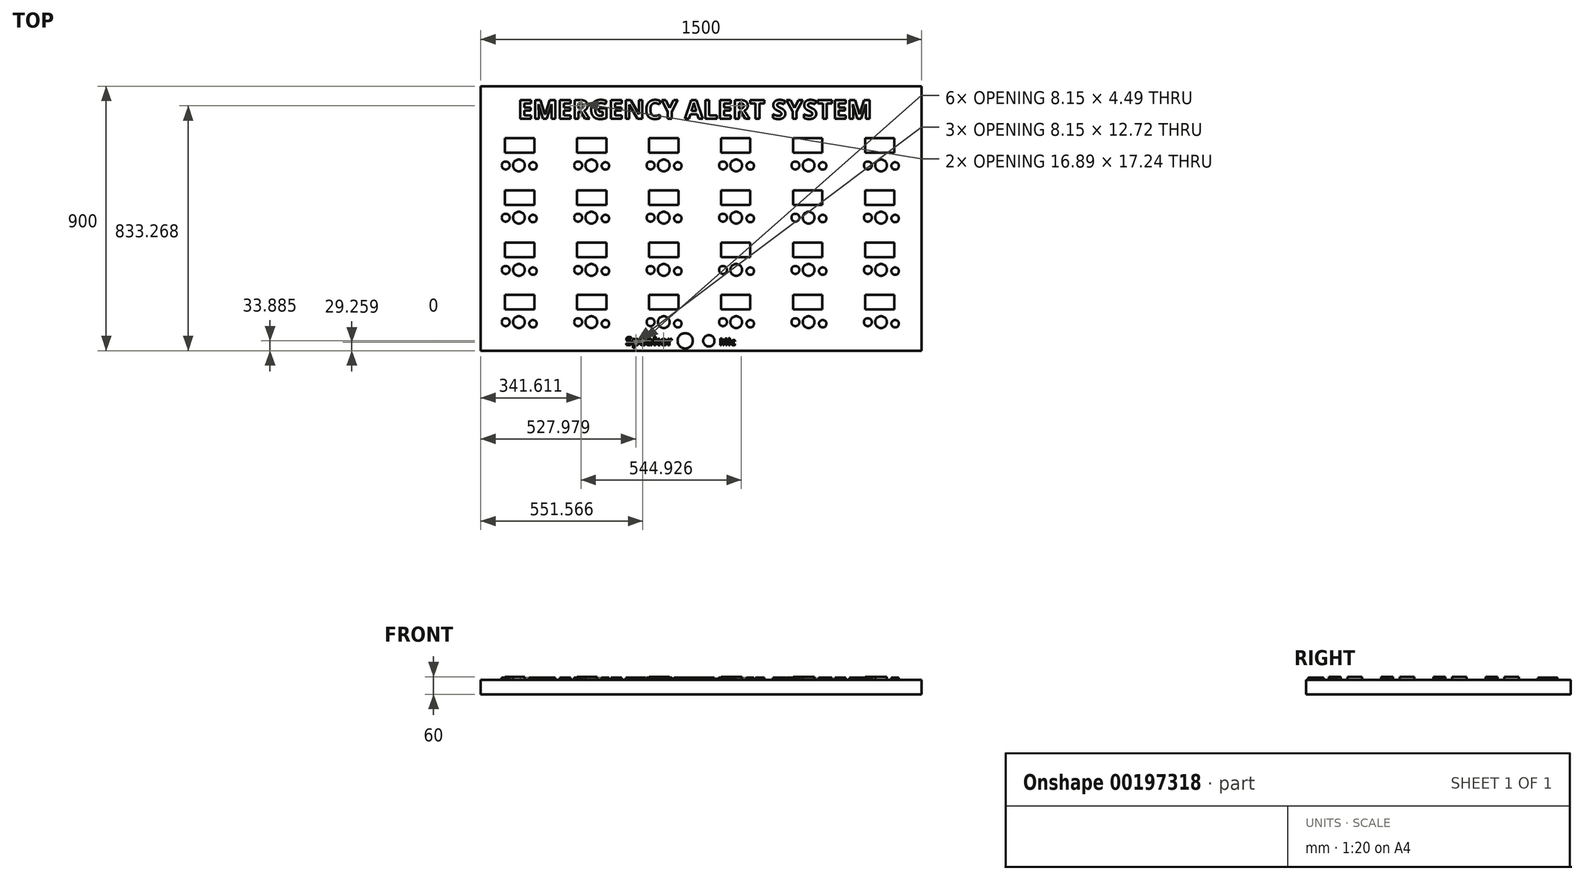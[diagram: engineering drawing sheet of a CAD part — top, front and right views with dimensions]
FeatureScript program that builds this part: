
annotation { "Feature Type Name" : "Feature", "Feature Type Description" : "" }
export const myFeature = defineFeature(function(context is Context, id is Id, definition is map)
    precondition{}
    {
        {
            var Q0;
            Q0=qCreatedBy(makeId("Top.planeOp"),FACE);
            var sketch = newSketch(context, id + "F0", { "sketchPlane" : qUnion([Q0])});
            skLineSegment(sketch, "E0.bottom", {"start": v(-750, 450) * mm, "end": v(750, 450) * mm});
            skLineSegment(sketch, "E0.top", {"start": v(-750, -450) * mm, "end": v(750, -450) * mm});
            skLineSegment(sketch, "E0.left", {"start": v(-750, 450) * mm, "end": v(-750, -450) * mm});
            skLineSegment(sketch, "E0.right", {"start": v(750, 450) * mm, "end": v(750, -450) * mm});
            skPoint(sketch, "E0.middle", {"position": v(0, 0) * mm});
            skSolve(sketch);
        }
        {
            var Q0;
            Q0=makeQuery(id+"F0.imprint","IMPRINT",FACE,{"disambiguationData":[TD([[makeQuery(id+"F0.imprint","IMPRINT",EDGE,{"derivedFrom":sQuery(id+"F0.wireOp",EDGE,"E0.bottom")}),-1.0]])]});
            extrude(context, id + "F1", {"entities" : qUnion([Q0]), "depth" : 50 * mm});
        }
        {
            var Q0;
            Q0=makeQuery(id+"F1.opExtrude","CAP_FACE",FACE,{"disambiguationData":[OSD([sQuery(id+"F0.wireOp",EDGE,"E0.bottom"),sQuery(id+"F0.wireOp",EDGE,"E0.top"),sQuery(id+"F0.wireOp",EDGE,"E0.left"),sQuery(id+"F0.wireOp",EDGE,"E0.right")])],"isStart":false});
            var sketch = newSketch(context, id + "F2", { "sketchPlane" : qUnion([Q0])});
            skLineSegment(sketch, "E1.bottom", {"start": v(-667.65, 273.63) * mm, "end": v(-567.65, 273.63) * mm});
            skLineSegment(sketch, "E1.top", {"start": v(-667.65, 223.63) * mm, "end": v(-567.65, 223.63) * mm});
            skLineSegment(sketch, "E1.left", {"start": v(-667.65, 273.63) * mm, "end": v(-667.65, 223.63) * mm});
            skLineSegment(sketch, "E1.right", {"start": v(-567.65, 273.63) * mm, "end": v(-567.65, 223.63) * mm});
            skLineSegment(sketch, "E2.0.1.0", {"start": v(-667.65, 95.83) * mm, "end": v(-567.65, 95.83) * mm});
            skLineSegment(sketch, "E2.0.1.1", {"start": v(-567.65, 95.83) * mm, "end": v(-567.65, 45.83) * mm});
            skLineSegment(sketch, "E2.0.1.2", {"start": v(-667.65, 45.83) * mm, "end": v(-567.65, 45.83) * mm});
            skLineSegment(sketch, "E2.0.1.3", {"start": v(-667.65, 95.83) * mm, "end": v(-667.65, 45.83) * mm});
            skLineSegment(sketch, "E2.0.2.0", {"start": v(-667.65, -81.97) * mm, "end": v(-567.65, -81.97) * mm});
            skLineSegment(sketch, "E2.0.2.1", {"start": v(-567.65, -81.97) * mm, "end": v(-567.65, -131.97) * mm});
            skLineSegment(sketch, "E2.0.2.2", {"start": v(-667.65, -131.97) * mm, "end": v(-567.65, -131.97) * mm});
            skLineSegment(sketch, "E2.0.2.3", {"start": v(-667.65, -81.97) * mm, "end": v(-667.65, -131.97) * mm});
            skLineSegment(sketch, "E2.0.3.0", {"start": v(-667.65, -259.77) * mm, "end": v(-567.65, -259.77) * mm});
            skLineSegment(sketch, "E2.0.3.1", {"start": v(-567.65, -259.77) * mm, "end": v(-567.65, -309.77) * mm});
            skLineSegment(sketch, "E2.0.3.2", {"start": v(-667.65, -309.77) * mm, "end": v(-567.65, -309.77) * mm});
            skLineSegment(sketch, "E2.0.3.3", {"start": v(-667.65, -259.77) * mm, "end": v(-667.65, -309.77) * mm});
            skLineSegment(sketch, "E2.1.0.0", {"start": v(-422.65, 273.63) * mm, "end": v(-322.65, 273.63) * mm});
            skLineSegment(sketch, "E2.1.0.1", {"start": v(-322.65, 273.63) * mm, "end": v(-322.65, 223.63) * mm});
            skLineSegment(sketch, "E2.1.0.2", {"start": v(-422.65, 223.63) * mm, "end": v(-322.65, 223.63) * mm});
            skLineSegment(sketch, "E2.1.0.3", {"start": v(-422.65, 273.63) * mm, "end": v(-422.65, 223.63) * mm});
            skLineSegment(sketch, "E2.1.1.0", {"start": v(-422.65, 95.83) * mm, "end": v(-322.65, 95.83) * mm});
            skLineSegment(sketch, "E2.1.1.1", {"start": v(-322.65, 95.83) * mm, "end": v(-322.65, 45.83) * mm});
            skLineSegment(sketch, "E2.1.1.2", {"start": v(-422.65, 45.83) * mm, "end": v(-322.65, 45.83) * mm});
            skLineSegment(sketch, "E2.1.1.3", {"start": v(-422.65, 95.83) * mm, "end": v(-422.65, 45.83) * mm});
            skLineSegment(sketch, "E2.1.2.0", {"start": v(-422.65, -81.97) * mm, "end": v(-322.65, -81.97) * mm});
            skLineSegment(sketch, "E2.1.2.1", {"start": v(-322.65, -81.97) * mm, "end": v(-322.65, -131.97) * mm});
            skLineSegment(sketch, "E2.1.2.2", {"start": v(-422.65, -131.97) * mm, "end": v(-322.65, -131.97) * mm});
            skLineSegment(sketch, "E2.1.2.3", {"start": v(-422.65, -81.97) * mm, "end": v(-422.65, -131.97) * mm});
            skLineSegment(sketch, "E2.1.3.0", {"start": v(-422.65, -259.77) * mm, "end": v(-322.65, -259.77) * mm});
            skLineSegment(sketch, "E2.1.3.1", {"start": v(-322.65, -259.77) * mm, "end": v(-322.65, -309.77) * mm});
            skLineSegment(sketch, "E2.1.3.2", {"start": v(-422.65, -309.77) * mm, "end": v(-322.65, -309.77) * mm});
            skLineSegment(sketch, "E2.1.3.3", {"start": v(-422.65, -259.77) * mm, "end": v(-422.65, -309.77) * mm});
            skLineSegment(sketch, "E2.2.0.0", {"start": v(-177.65, 273.63) * mm, "end": v(-77.65, 273.63) * mm});
            skLineSegment(sketch, "E2.2.0.1", {"start": v(-77.65, 273.63) * mm, "end": v(-77.65, 223.63) * mm});
            skLineSegment(sketch, "E2.2.0.2", {"start": v(-177.65, 223.63) * mm, "end": v(-77.65, 223.63) * mm});
            skLineSegment(sketch, "E2.2.0.3", {"start": v(-177.65, 273.63) * mm, "end": v(-177.65, 223.63) * mm});
            skLineSegment(sketch, "E2.2.1.0", {"start": v(-177.65, 95.83) * mm, "end": v(-77.65, 95.83) * mm});
            skLineSegment(sketch, "E2.2.1.1", {"start": v(-77.65, 95.83) * mm, "end": v(-77.65, 45.83) * mm});
            skLineSegment(sketch, "E2.2.1.2", {"start": v(-177.65, 45.83) * mm, "end": v(-77.65, 45.83) * mm});
            skLineSegment(sketch, "E2.2.1.3", {"start": v(-177.65, 95.83) * mm, "end": v(-177.65, 45.83) * mm});
            skLineSegment(sketch, "E2.2.2.0", {"start": v(-177.65, -81.97) * mm, "end": v(-77.65, -81.97) * mm});
            skLineSegment(sketch, "E2.2.2.1", {"start": v(-77.65, -81.97) * mm, "end": v(-77.65, -131.97) * mm});
            skLineSegment(sketch, "E2.2.2.2", {"start": v(-177.65, -131.97) * mm, "end": v(-77.65, -131.97) * mm});
            skLineSegment(sketch, "E2.2.2.3", {"start": v(-177.65, -81.97) * mm, "end": v(-177.65, -131.97) * mm});
            skLineSegment(sketch, "E2.2.3.0", {"start": v(-177.65, -259.77) * mm, "end": v(-77.65, -259.77) * mm});
            skLineSegment(sketch, "E2.2.3.1", {"start": v(-77.65, -259.77) * mm, "end": v(-77.65, -309.77) * mm});
            skLineSegment(sketch, "E2.2.3.2", {"start": v(-177.65, -309.77) * mm, "end": v(-77.65, -309.77) * mm});
            skLineSegment(sketch, "E2.2.3.3", {"start": v(-177.65, -259.77) * mm, "end": v(-177.65, -309.77) * mm});
            skLineSegment(sketch, "E2.3.0.0", {"start": v(67.35, 273.63) * mm, "end": v(167.35, 273.63) * mm});
            skLineSegment(sketch, "E2.3.0.1", {"start": v(167.35, 273.63) * mm, "end": v(167.35, 223.63) * mm});
            skLineSegment(sketch, "E2.3.0.2", {"start": v(67.35, 223.63) * mm, "end": v(167.35, 223.63) * mm});
            skLineSegment(sketch, "E2.3.0.3", {"start": v(67.35, 273.63) * mm, "end": v(67.35, 223.63) * mm});
            skLineSegment(sketch, "E2.3.1.0", {"start": v(67.35, 95.83) * mm, "end": v(167.35, 95.83) * mm});
            skLineSegment(sketch, "E2.3.1.1", {"start": v(167.35, 95.83) * mm, "end": v(167.35, 45.83) * mm});
            skLineSegment(sketch, "E2.3.1.2", {"start": v(67.35, 45.83) * mm, "end": v(167.35, 45.83) * mm});
            skLineSegment(sketch, "E2.3.1.3", {"start": v(67.35, 95.83) * mm, "end": v(67.35, 45.83) * mm});
            skLineSegment(sketch, "E2.3.2.0", {"start": v(67.35, -81.97) * mm, "end": v(167.35, -81.97) * mm});
            skLineSegment(sketch, "E2.3.2.1", {"start": v(167.35, -81.97) * mm, "end": v(167.35, -131.97) * mm});
            skLineSegment(sketch, "E2.3.2.2", {"start": v(67.35, -131.97) * mm, "end": v(167.35, -131.97) * mm});
            skLineSegment(sketch, "E2.3.2.3", {"start": v(67.35, -81.97) * mm, "end": v(67.35, -131.97) * mm});
            skLineSegment(sketch, "E2.3.3.0", {"start": v(67.35, -259.77) * mm, "end": v(167.35, -259.77) * mm});
            skLineSegment(sketch, "E2.3.3.1", {"start": v(167.35, -259.77) * mm, "end": v(167.35, -309.77) * mm});
            skLineSegment(sketch, "E2.3.3.2", {"start": v(67.35, -309.77) * mm, "end": v(167.35, -309.77) * mm});
            skLineSegment(sketch, "E2.3.3.3", {"start": v(67.35, -259.77) * mm, "end": v(67.35, -309.77) * mm});
            skLineSegment(sketch, "E2.4.0.0", {"start": v(312.35, 273.63) * mm, "end": v(412.35, 273.63) * mm});
            skLineSegment(sketch, "E2.4.0.1", {"start": v(412.35, 273.63) * mm, "end": v(412.35, 223.63) * mm});
            skLineSegment(sketch, "E2.4.0.2", {"start": v(312.35, 223.63) * mm, "end": v(412.35, 223.63) * mm});
            skLineSegment(sketch, "E2.4.0.3", {"start": v(312.35, 273.63) * mm, "end": v(312.35, 223.63) * mm});
            skLineSegment(sketch, "E2.4.1.0", {"start": v(312.35, 95.83) * mm, "end": v(412.35, 95.83) * mm});
            skLineSegment(sketch, "E2.4.1.1", {"start": v(412.35, 95.83) * mm, "end": v(412.35, 45.83) * mm});
            skLineSegment(sketch, "E2.4.1.2", {"start": v(312.35, 45.83) * mm, "end": v(412.35, 45.83) * mm});
            skLineSegment(sketch, "E2.4.1.3", {"start": v(312.35, 95.83) * mm, "end": v(312.35, 45.83) * mm});
            skLineSegment(sketch, "E2.4.2.0", {"start": v(312.35, -81.97) * mm, "end": v(412.35, -81.97) * mm});
            skLineSegment(sketch, "E2.4.2.1", {"start": v(412.35, -81.97) * mm, "end": v(412.35, -131.97) * mm});
            skLineSegment(sketch, "E2.4.2.2", {"start": v(312.35, -131.97) * mm, "end": v(412.35, -131.97) * mm});
            skLineSegment(sketch, "E2.4.2.3", {"start": v(312.35, -81.97) * mm, "end": v(312.35, -131.97) * mm});
            skLineSegment(sketch, "E2.4.3.0", {"start": v(312.35, -259.77) * mm, "end": v(412.35, -259.77) * mm});
            skLineSegment(sketch, "E2.4.3.1", {"start": v(412.35, -259.77) * mm, "end": v(412.35, -309.77) * mm});
            skLineSegment(sketch, "E2.4.3.2", {"start": v(312.35, -309.77) * mm, "end": v(412.35, -309.77) * mm});
            skLineSegment(sketch, "E2.4.3.3", {"start": v(312.35, -259.77) * mm, "end": v(312.35, -309.77) * mm});
            skLineSegment(sketch, "E2.5.0.0", {"start": v(557.35, 273.63) * mm, "end": v(657.35, 273.63) * mm});
            skLineSegment(sketch, "E2.5.0.1", {"start": v(657.35, 273.63) * mm, "end": v(657.35, 223.63) * mm});
            skLineSegment(sketch, "E2.5.0.2", {"start": v(557.35, 223.63) * mm, "end": v(657.35, 223.63) * mm});
            skLineSegment(sketch, "E2.5.0.3", {"start": v(557.35, 273.63) * mm, "end": v(557.35, 223.63) * mm});
            skLineSegment(sketch, "E2.5.1.0", {"start": v(557.35, 95.83) * mm, "end": v(657.35, 95.83) * mm});
            skLineSegment(sketch, "E2.5.1.1", {"start": v(657.35, 95.83) * mm, "end": v(657.35, 45.83) * mm});
            skLineSegment(sketch, "E2.5.1.2", {"start": v(557.35, 45.83) * mm, "end": v(657.35, 45.83) * mm});
            skLineSegment(sketch, "E2.5.1.3", {"start": v(557.35, 95.83) * mm, "end": v(557.35, 45.83) * mm});
            skLineSegment(sketch, "E2.5.2.0", {"start": v(557.35, -81.97) * mm, "end": v(657.35, -81.97) * mm});
            skLineSegment(sketch, "E2.5.2.1", {"start": v(657.35, -81.97) * mm, "end": v(657.35, -131.97) * mm});
            skLineSegment(sketch, "E2.5.2.2", {"start": v(557.35, -131.97) * mm, "end": v(657.35, -131.97) * mm});
            skLineSegment(sketch, "E2.5.2.3", {"start": v(557.35, -81.97) * mm, "end": v(557.35, -131.97) * mm});
            skLineSegment(sketch, "E2.5.3.0", {"start": v(557.35, -259.77) * mm, "end": v(657.35, -259.77) * mm});
            skLineSegment(sketch, "E2.5.3.1", {"start": v(657.35, -259.77) * mm, "end": v(657.35, -309.77) * mm});
            skLineSegment(sketch, "E2.5.3.2", {"start": v(557.35, -309.77) * mm, "end": v(657.35, -309.77) * mm});
            skLineSegment(sketch, "E2.5.3.3", {"start": v(557.35, -259.77) * mm, "end": v(557.35, -309.77) * mm});
            skLineSegment(sketch, "E2.direction1", {"start": v(-667.65, 273.63) * mm, "end": v(-422.65, 273.63) * mm, "construction": true});
            skLineSegment(sketch, "E2.direction2", {"start": v(-667.65, 273.63) * mm, "end": v(-667.65, 95.83) * mm, "construction": true});
            skSolve(sketch);
        }
        {
            var Q0;
            Q0 = qSketchRegion(id + "F2", true);
            extrude(context, id + "F3", {"entities" : qUnion([Q0]), "depth" : 10 * mm});
        }
        {
            var Q0;
            Q0=makeQuery(id+"F1.opExtrude","CAP_FACE",FACE,{"disambiguationData":[OSD([sQuery(id+"F0.wireOp",EDGE,"E0.bottom"),sQuery(id+"F0.wireOp",EDGE,"E0.top"),sQuery(id+"F0.wireOp",EDGE,"E0.left"),sQuery(id+"F0.wireOp",EDGE,"E0.right")])],"isStart":false});
            var sketch = newSketch(context, id + "F4", { "sketchPlane" : qUnion([Q0])});
            skCircle(sketch, "E3", {"center": v(-619.9, 180.43) * mm, "radius": 20.14 * mm});
            skCircle(sketch, "E4.0.1.0", {"center": v(-619.9, 2.63) * mm, "radius": 20.14 * mm});
            skCircle(sketch, "E4.0.2.0", {"center": v(-619.9, -175.17) * mm, "radius": 20.14 * mm});
            skCircle(sketch, "E4.0.3.0", {"center": v(-619.9, -352.97) * mm, "radius": 20.14 * mm});
            skCircle(sketch, "E4.1.0.0", {"center": v(-373.51, 180.43) * mm, "radius": 20.14 * mm});
            skCircle(sketch, "E4.1.1.0", {"center": v(-373.51, 2.63) * mm, "radius": 20.14 * mm});
            skCircle(sketch, "E4.1.2.0", {"center": v(-373.51, -175.17) * mm, "radius": 20.14 * mm});
            skCircle(sketch, "E4.1.3.0", {"center": v(-373.51, -352.97) * mm, "radius": 20.14 * mm});
            skCircle(sketch, "E4.2.0.0", {"center": v(-127.13, 180.43) * mm, "radius": 20.14 * mm});
            skCircle(sketch, "E4.2.1.0", {"center": v(-127.13, 2.63) * mm, "radius": 20.14 * mm});
            skCircle(sketch, "E4.2.2.0", {"center": v(-127.13, -175.17) * mm, "radius": 20.14 * mm});
            skCircle(sketch, "E4.2.3.0", {"center": v(-127.13, -352.97) * mm, "radius": 20.14 * mm});
            skCircle(sketch, "E4.3.0.0", {"center": v(119.25, 180.43) * mm, "radius": 20.14 * mm});
            skCircle(sketch, "E4.3.1.0", {"center": v(119.25, 2.63) * mm, "radius": 20.14 * mm});
            skCircle(sketch, "E4.3.2.0", {"center": v(119.25, -175.17) * mm, "radius": 20.14 * mm});
            skCircle(sketch, "E4.3.3.0", {"center": v(119.25, -352.97) * mm, "radius": 20.14 * mm});
            skCircle(sketch, "E4.4.0.0", {"center": v(365.63, 180.43) * mm, "radius": 20.14 * mm});
            skCircle(sketch, "E4.4.1.0", {"center": v(365.63, 2.63) * mm, "radius": 20.14 * mm});
            skCircle(sketch, "E4.4.2.0", {"center": v(365.63, -175.17) * mm, "radius": 20.14 * mm});
            skCircle(sketch, "E4.4.3.0", {"center": v(365.63, -352.97) * mm, "radius": 20.14 * mm});
            skCircle(sketch, "E4.5.0.0", {"center": v(612, 180.43) * mm, "radius": 20.14 * mm});
            skCircle(sketch, "E4.5.1.0", {"center": v(612, 2.63) * mm, "radius": 20.14 * mm});
            skCircle(sketch, "E4.5.2.0", {"center": v(612, -175.17) * mm, "radius": 20.14 * mm});
            skCircle(sketch, "E4.5.3.0", {"center": v(612, -352.97) * mm, "radius": 20.14 * mm});
            skLineSegment(sketch, "E4.direction1", {"start": v(-619.9, 180.43) * mm, "end": v(-373.51, 180.43) * mm, "construction": true});
            skLineSegment(sketch, "E4.direction2", {"start": v(-619.9, 180.43) * mm, "end": v(-619.9, 2.63) * mm, "construction": true});
            skSolve(sketch);
        }
        {
            var Q0;
            Q0 = qSketchRegion(id + "F4", true);
            extrude(context, id + "F5", {"entities" : qUnion([Q0]), "depth" : 10 * mm});
        }
        {
            var Q0;
            Q0=makeQuery(id+"F1.opExtrude","CAP_FACE",FACE,{"disambiguationData":[OSD([sQuery(id+"F0.wireOp",EDGE,"E0.bottom"),sQuery(id+"F0.wireOp",EDGE,"E0.top"),sQuery(id+"F0.wireOp",EDGE,"E0.left"),sQuery(id+"F0.wireOp",EDGE,"E0.right")])],"isStart":false});
            var sketch = newSketch(context, id + "F6", { "sketchPlane" : qUnion([Q0])});
            skSolve(sketch);
        }
        {
            var Q0;
            Q0=makeQuery(id+"F6.imprint","IMPRINT",FACE,{"disambiguationData":[TD([[makeQuery(id+"F6.imprint","IMPRINT",EDGE,{"derivedFrom":makeQuery(id+"F1.opExtrude","CAP_EDGE",EDGE,{"disambiguationData":[OSD([sQuery(id+"F0.wireOp",EDGE,"E0.bottom")])],"isStart":false})}),-1.0]])]});
            var sketch = newSketch(context, id + "F7", { "sketchPlane" : qUnion([Q0])});
            skCircle(sketch, "E5", {"center": v(-571.98, 178.93) * mm, "radius": 12.7 * mm});
            skCircle(sketch, "E6.0.1.0", {"center": v(-571.98, -0.14) * mm, "radius": 12.7 * mm});
            skCircle(sketch, "E6.0.2.0", {"center": v(-571.98, -179.2) * mm, "radius": 12.7 * mm});
            skCircle(sketch, "E6.0.3.0", {"center": v(-571.98, -358.28) * mm, "radius": 12.7 * mm});
            skCircle(sketch, "E6.1.0.0", {"center": v(-325.6, 178.93) * mm, "radius": 12.7 * mm});
            skCircle(sketch, "E6.1.1.0", {"center": v(-325.6, -0.14) * mm, "radius": 12.7 * mm});
            skCircle(sketch, "E6.1.2.0", {"center": v(-325.6, -179.2) * mm, "radius": 12.7 * mm});
            skCircle(sketch, "E6.1.3.0", {"center": v(-325.6, -358.28) * mm, "radius": 12.7 * mm});
            skCircle(sketch, "E6.2.0.0", {"center": v(-79.22, 178.93) * mm, "radius": 12.7 * mm});
            skCircle(sketch, "E6.2.1.0", {"center": v(-79.22, -0.14) * mm, "radius": 12.7 * mm});
            skCircle(sketch, "E6.2.2.0", {"center": v(-79.22, -179.2) * mm, "radius": 12.7 * mm});
            skCircle(sketch, "E6.2.3.0", {"center": v(-79.22, -358.28) * mm, "radius": 12.7 * mm});
            skCircle(sketch, "E6.3.0.0", {"center": v(167.16, 178.93) * mm, "radius": 12.7 * mm});
            skCircle(sketch, "E6.3.1.0", {"center": v(167.16, -0.14) * mm, "radius": 12.7 * mm});
            skCircle(sketch, "E6.3.2.0", {"center": v(167.16, -179.2) * mm, "radius": 12.7 * mm});
            skCircle(sketch, "E6.3.3.0", {"center": v(167.16, -358.28) * mm, "radius": 12.7 * mm});
            skCircle(sketch, "E6.4.0.0", {"center": v(413.54, 178.93) * mm, "radius": 12.7 * mm});
            skCircle(sketch, "E6.4.1.0", {"center": v(413.54, -0.14) * mm, "radius": 12.7 * mm});
            skCircle(sketch, "E6.4.2.0", {"center": v(413.54, -179.2) * mm, "radius": 12.7 * mm});
            skCircle(sketch, "E6.4.3.0", {"center": v(413.54, -358.28) * mm, "radius": 12.7 * mm});
            skCircle(sketch, "E6.5.0.0", {"center": v(659.92, 178.93) * mm, "radius": 12.7 * mm});
            skCircle(sketch, "E6.5.1.0", {"center": v(659.92, -0.14) * mm, "radius": 12.7 * mm});
            skCircle(sketch, "E6.5.2.0", {"center": v(659.92, -179.2) * mm, "radius": 12.7 * mm});
            skCircle(sketch, "E6.5.3.0", {"center": v(659.92, -358.28) * mm, "radius": 12.7 * mm});
            skLineSegment(sketch, "E6.direction1", {"start": v(-571.98, 178.93) * mm, "end": v(-325.6, 178.93) * mm, "construction": true});
            skLineSegment(sketch, "E6.direction2", {"start": v(-571.98, 178.93) * mm, "end": v(-571.98, -0.14) * mm, "construction": true});
            skSolve(sketch);
        }
        {
            var Q0;
            Q0 = qSketchRegion(id + "F7", true);
            extrude(context, id + "F8", {"entities" : qUnion([Q0]), "depth" : 7 * mm});
        }
        {
            var Q0;
            Q0=makeQuery(id+"F6.imprint","IMPRINT",FACE,{"disambiguationData":[TD([[makeQuery(id+"F6.imprint","IMPRINT",EDGE,{"derivedFrom":makeQuery(id+"F1.opExtrude","CAP_EDGE",EDGE,{"disambiguationData":[OSD([sQuery(id+"F0.wireOp",EDGE,"E0.bottom")])],"isStart":false})}),-1.0]])]});
            var sketch = newSketch(context, id + "F9", { "sketchPlane" : qUnion([Q0])});
            skCircle(sketch, "E7", {"center": v(-664.81, 180.43) * mm, "radius": 13.56 * mm});
            skCircle(sketch, "E8.0.1.0", {"center": v(-664.81, 2.63) * mm, "radius": 13.56 * mm});
            skCircle(sketch, "E8.0.2.0", {"center": v(-664.81, -175.17) * mm, "radius": 13.56 * mm});
            skCircle(sketch, "E8.0.3.0", {"center": v(-664.81, -352.97) * mm, "radius": 13.56 * mm});
            skCircle(sketch, "E8.1.0.0", {"center": v(-418.43, 180.43) * mm, "radius": 13.56 * mm});
            skCircle(sketch, "E8.1.1.0", {"center": v(-418.43, 2.63) * mm, "radius": 13.56 * mm});
            skCircle(sketch, "E8.1.2.0", {"center": v(-418.43, -175.17) * mm, "radius": 13.56 * mm});
            skCircle(sketch, "E8.1.3.0", {"center": v(-418.43, -352.97) * mm, "radius": 13.56 * mm});
            skCircle(sketch, "E8.2.0.0", {"center": v(-172.05, 180.43) * mm, "radius": 13.56 * mm});
            skCircle(sketch, "E8.2.1.0", {"center": v(-172.05, 2.63) * mm, "radius": 13.56 * mm});
            skCircle(sketch, "E8.2.2.0", {"center": v(-172.05, -175.17) * mm, "radius": 13.56 * mm});
            skCircle(sketch, "E8.2.3.0", {"center": v(-172.05, -352.97) * mm, "radius": 13.56 * mm});
            skCircle(sketch, "E8.3.0.0", {"center": v(74.33, 180.43) * mm, "radius": 13.56 * mm});
            skCircle(sketch, "E8.3.1.0", {"center": v(74.33, 2.63) * mm, "radius": 13.56 * mm});
            skCircle(sketch, "E8.3.2.0", {"center": v(74.33, -175.17) * mm, "radius": 13.56 * mm});
            skCircle(sketch, "E8.3.3.0", {"center": v(74.33, -352.97) * mm, "radius": 13.56 * mm});
            skCircle(sketch, "E8.4.0.0", {"center": v(320.7, 180.43) * mm, "radius": 13.56 * mm});
            skCircle(sketch, "E8.4.1.0", {"center": v(320.7, 2.63) * mm, "radius": 13.56 * mm});
            skCircle(sketch, "E8.4.2.0", {"center": v(320.7, -175.17) * mm, "radius": 13.56 * mm});
            skCircle(sketch, "E8.4.3.0", {"center": v(320.7, -352.97) * mm, "radius": 13.56 * mm});
            skCircle(sketch, "E8.5.0.0", {"center": v(567.09, 180.43) * mm, "radius": 13.56 * mm});
            skCircle(sketch, "E8.5.1.0", {"center": v(567.09, 2.63) * mm, "radius": 13.56 * mm});
            skCircle(sketch, "E8.5.2.0", {"center": v(567.09, -175.17) * mm, "radius": 13.56 * mm});
            skCircle(sketch, "E8.5.3.0", {"center": v(567.09, -352.97) * mm, "radius": 13.56 * mm});
            skLineSegment(sketch, "E8.direction1", {"start": v(-664.81, 180.43) * mm, "end": v(-418.43, 180.43) * mm, "construction": true});
            skLineSegment(sketch, "E8.direction2", {"start": v(-664.81, 180.43) * mm, "end": v(-664.81, 2.63) * mm, "construction": true});
            skSolve(sketch);
        }
        {
            var Q0;
            Q0 = qSketchRegion(id + "F9", true);
            extrude(context, id + "F10", {"entities" : qUnion([Q0]), "depth" : 7 * mm});
        }
        {
            var Q0;
            Q0=makeQuery(id+"F6.imprint","IMPRINT",FACE,{"disambiguationData":[TD([[makeQuery(id+"F6.imprint","IMPRINT",EDGE,{"derivedFrom":makeQuery(id+"F1.opExtrude","CAP_EDGE",EDGE,{"disambiguationData":[OSD([sQuery(id+"F0.wireOp",EDGE,"E0.bottom")])],"isStart":false})}),-1.0]])]});
            var sketch = newSketch(context, id + "F11", { "sketchPlane" : qUnion([Q0])});
            skText(sketch, "E9", { "text": "EMERGENCY ALERT SYSTEM", "fontName": "OpenSans-Bold.ttf"});
            const initialGuessF11  = {"E9": [-0.62289, 0.33914, 1, 0, 0.06439]};
            skSetInitialGuess(sketch, initialGuessF11);
            skSolve(sketch);
        }
        {
            var Q0;
            Q0 = qSketchRegion(id + "F11", true);
            extrude(context, id + "F12", {"entities" : qUnion([Q0]), "depth" : 7 * mm});
        }
        {
            var Q0;
            Q0=makeQuery(id+"F6.imprint","IMPRINT",FACE,{"disambiguationData":[TD([[makeQuery(id+"F6.imprint","IMPRINT",EDGE,{"derivedFrom":makeQuery(id+"F1.opExtrude","CAP_EDGE",EDGE,{"disambiguationData":[OSD([sQuery(id+"F0.wireOp",EDGE,"E0.bottom")])],"isStart":false})}),-1.0]])]});
            var sketch = newSketch(context, id + "F13", { "sketchPlane" : qUnion([Q0])});
            skCircle(sketch, "E10", {"center": v(-54.28, -416.44) * mm, "radius": 26 * mm});
            skSolve(sketch);
        }
        {
            var Q0;
            Q0 = qSketchRegion(id + "F13", true);
            extrude(context, id + "F14", {"entities" : qUnion([Q0]), "depth" : 7 * mm});
        }
        {
            var Q0;
            Q0=makeQuery(id+"F6.imprint","IMPRINT",FACE,{"disambiguationData":[TD([[makeQuery(id+"F6.imprint","IMPRINT",EDGE,{"derivedFrom":makeQuery(id+"F1.opExtrude","CAP_EDGE",EDGE,{"disambiguationData":[OSD([sQuery(id+"F0.wireOp",EDGE,"E0.bottom")])],"isStart":false})}),-1.0]])]});
            var sketch = newSketch(context, id + "F15", { "sketchPlane" : qUnion([Q0])});
            skCircle(sketch, "E11", {"center": v(26.2, -416.44) * mm, "radius": 19.27 * mm});
            skSolve(sketch);
        }
        {
            var Q0;
            Q0 = qSketchRegion(id + "F15", true);
            extrude(context, id + "F16", {"entities" : qUnion([Q0]), "depth" : 7 * mm});
        }
        {
            var Q0;
            Q0=makeQuery(id+"F6.imprint","IMPRINT",FACE,{"disambiguationData":[TD([[makeQuery(id+"F6.imprint","IMPRINT",EDGE,{"derivedFrom":makeQuery(id+"F1.opExtrude","CAP_EDGE",EDGE,{"disambiguationData":[OSD([sQuery(id+"F0.wireOp",EDGE,"E0.bottom")])],"isStart":false})}),-1.0]])]});
            var sketch = newSketch(context, id + "F17", { "sketchPlane" : qUnion([Q0])});
            skText(sketch, "E12", { "text": "Speaker", "fontName": "OpenSans-Bold.ttf"});
            const initialGuessF17  = {"E12": [-0.25642, -0.43142, 1, 0, 0.02807]};
            skSetInitialGuess(sketch, initialGuessF17);
            skSolve(sketch);
        }
        {
            var Q0;
            Q0 = qSketchRegion(id + "F17", true);
            extrude(context, id + "F18", {"entities" : qUnion([Q0]), "depth" : 7 * mm});
        }
        {
            var Q0;
            Q0=makeQuery(id+"F6.imprint","IMPRINT",FACE,{"disambiguationData":[TD([[makeQuery(id+"F6.imprint","IMPRINT",EDGE,{"derivedFrom":makeQuery(id+"F1.opExtrude","CAP_EDGE",EDGE,{"disambiguationData":[OSD([sQuery(id+"F0.wireOp",EDGE,"E0.bottom")])],"isStart":false})}),-1.0]])]});
            var sketch = newSketch(context, id + "F19", { "sketchPlane" : qUnion([Q0])});
            skText(sketch, "E13", { "text": "Mic", "fontName": "OpenSans-Bold.ttf"});
            const initialGuessF19  = {"E13": [0.06176, -0.43142, 1, 0, 0.02246]};
            skSetInitialGuess(sketch, initialGuessF19);
            skSolve(sketch);
        }
        {
            var Q0;
            Q0 = qSketchRegion(id + "F19", true);
            extrude(context, id + "F20", {"entities" : qUnion([Q0]), "depth" : 7 * mm});
        }
        {
            var Q0;
            Q0 = qSketchRegion(id + "F17", true);
            extrude(context, id + "F21", {"entities" : qUnion([Q0]), "depth" : 7 * mm});
        }
        {
            var Q0;
            Q0 = qSketchRegion(id + "F17", true);
            extrude(context, id + "F22", {"entities" : qUnion([Q0]), "depth" : 7 * mm});
        }
    });
